# Revit family: Sanitary_Basins_Sanindusa_Comby -Wash-Basin-To-Place
name_source: partatom
category: Plumbing Fixtures
revit_build: Autodesk Revit 2018 (Build: 20170223_1515(x64)
units: mm (PartAtom-declared; Revit-internal decimal feet)

## family parameters
Always vertical = Yes
Cut with Voids When Loaded = No
OmniClass Number = 23.45.00.00
OmniClass Title = Sanitary, Laundry, and Cleaning Equipment
Part Type = Normal
Room Calculation Point = No
Round Connector Dimension = Use Diameter
Shared = No
Work Plane-Based = No

## types (1)
- SanindusaWashBasin108660004
    AssetType = Fixed
    Category = Pr_40_20_96_18: Counter top wash basins
    CodePerformance = EN 14688:2015 CL00, EN 14688:2015, EN 14688:2015, EN 14688:2015
    Color = white
    Constituents = 6A8606-comby cup holder accessory (not included),6A8600-comby cup (not included), 6A8605- comby single accessory (not included), 4V9711-unslotted waste for basin without overflow (not included)
    Cost = 0 $
    Description = wash basin to place with flap
    DrainSize = 47 mm  [stored 0.154199 ft]
    Edition number = 1
    Features = With optional wood accessories, and a glass cup, very usefull on the day-to-day hygiene. The wash basin has a built-in place where objects can be laid.
    Finish = gloss
    InstallationDate = 1900-12-31T23:59:59
    Manufacturer = Sanindusa
    ManufacturerName = Sanindusa
    ManufacturerURL = www.tec.sanindusa.pt
    Material = vitreous china
    ModelNumber = 108660004
    ModelReference = Comby
    Name = Comby 61x41 wash basin to place
    NominalHeight = 220 mm  [stored 0.721785 ft]
    NominalLength = 610 mm  [stored 2.00131 ft]
    NominalWidth = 405 mm
    Product Guid = 41e5f9ea-77f5-4533-a973-031aa7032e27
    Product data url = https://bimobject.com
    ProductInformation = https://www.tec.sanindusa.pt
    ProductionYear = 2017
    Shape = rectangular
    Size = 61x41
    SpilloverLevel = 135 mm  [stored 0.442913 ft]
    URL = www.tec.sanindusa.pt
    Uniclass2015Code = Pr_40_20_96_18
    Uniclass2015Title = Counter top wash basins
    Uniclass2015Version = Products v1.6
    Version = 2
    WarrantyDescription = https://www.tec.sanindusa.pt
    WarrantyDurationParts = 5
    WarrantyDurationUnit = year
    WarrantyStartDate = 1900-12-31T23:59:59
1900-12-31T23:59:59
    WashHandBasinMounting = other
    WashHandBasinType = other
    Weight = 23.20 kg

note: [stored X ft] marks values corroborated as IEEE doubles in the binary element streams (Revit-internal decimal feet)

## geometry (parser evidence)
native form markers: Blend x2, Sweep x8
no freeform markers — native parametric forms only
